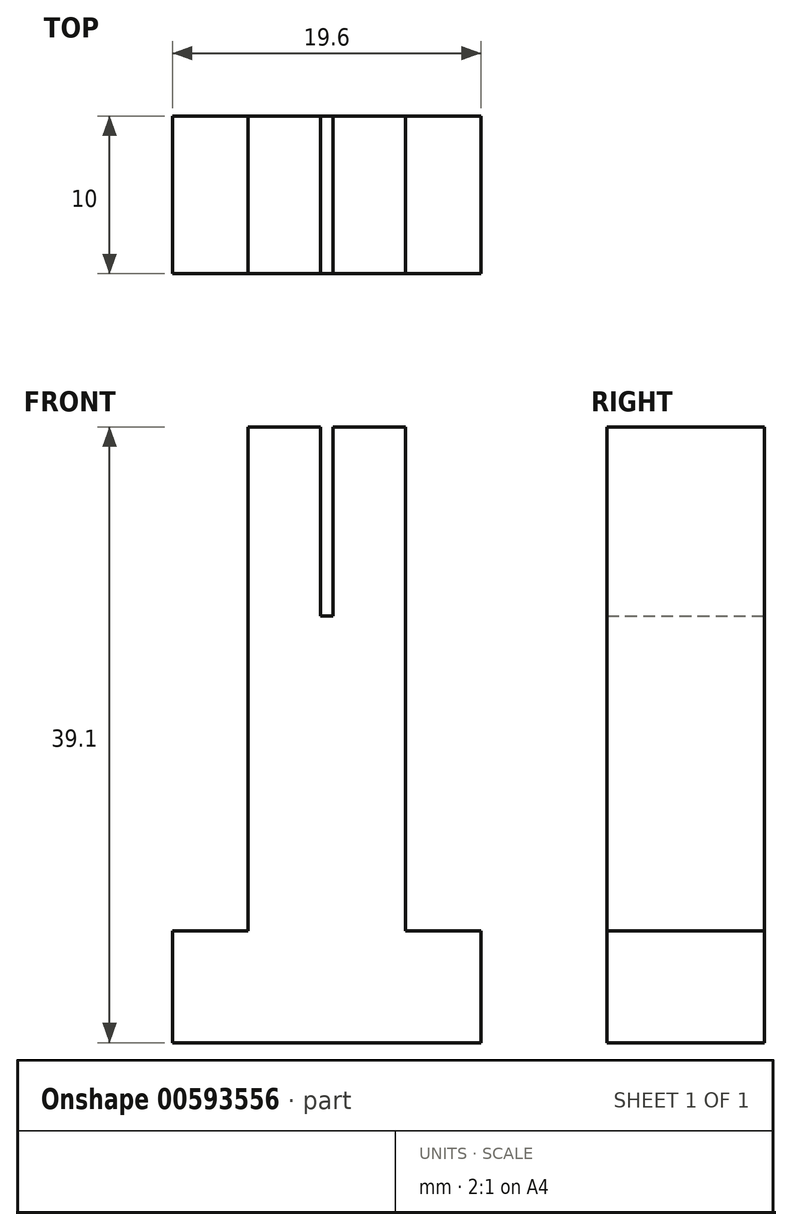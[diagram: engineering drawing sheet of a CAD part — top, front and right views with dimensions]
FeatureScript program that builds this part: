
annotation { "Feature Type Name" : "Feature", "Feature Type Description" : "" }
export const myFeature = defineFeature(function(context is Context, id is Id, definition is map)
    precondition{}
    {
        {
            var Q0;
            Q0=qCreatedBy(makeId("Front.planeOp"),FACE);
            var sketch = newSketch(context, id + "F0", { "sketchPlane" : qUnion([Q0])});
            skLineSegment(sketch, "E0", {"start": v(-9.8, 0) * mm, "end": v(-9.8, 7.1) * mm});
            skLineSegment(sketch, "E1", {"start": v(-9.8, 7.1) * mm, "end": v(-5, 7.1) * mm});
            skLineSegment(sketch, "E2", {"start": v(0.4, 27.1) * mm, "end": v(0.4, 39.1) * mm});
            skLineSegment(sketch, "E3", {"start": v(0.4, 39.1) * mm, "end": v(5, 39.1) * mm});
            skLineSegment(sketch, "E4", {"start": v(5, 39.1) * mm, "end": v(5, 7.1) * mm});
            skLineSegment(sketch, "E5", {"start": v(5, 7.1) * mm, "end": v(9.8, 7.1) * mm});
            skLineSegment(sketch, "E6", {"start": v(9.8, 7.1) * mm, "end": v(9.8, 0) * mm});
            skLineSegment(sketch, "E7", {"start": v(9.8, 0) * mm, "end": v(-9.8, 0) * mm});
            skLineSegment(sketch, "E8", {"start": v(0.4, 27.1) * mm, "end": v(-0.4, 27.1) * mm});
            skLineSegment(sketch, "E9", {"start": v(-0.4, 27.1) * mm, "end": v(-0.4, 39.1) * mm});
            skLineSegment(sketch, "E10", {"start": v(-0.4, 39.1) * mm, "end": v(-5, 39.1) * mm});
            skLineSegment(sketch, "E11", {"start": v(-5, 39.1) * mm, "end": v(-5, 7.1) * mm});
            skSolve(sketch);
        }
        {
            var Q0;
            Q0=makeQuery(id+"F0.imprint","IMPRINT",FACE,{"disambiguationData":[TD([[makeQuery(id+"F0.imprint","IMPRINT",EDGE,{"derivedFrom":sQuery(id+"F0.wireOp",EDGE,"E0")}),-1.0]])]});
            extrude(context, id + "F1", {"entities" : qUnion([Q0]), "depth" : 10 * mm, "offsetDistance" : 25.4 * mm});
        }
    });
